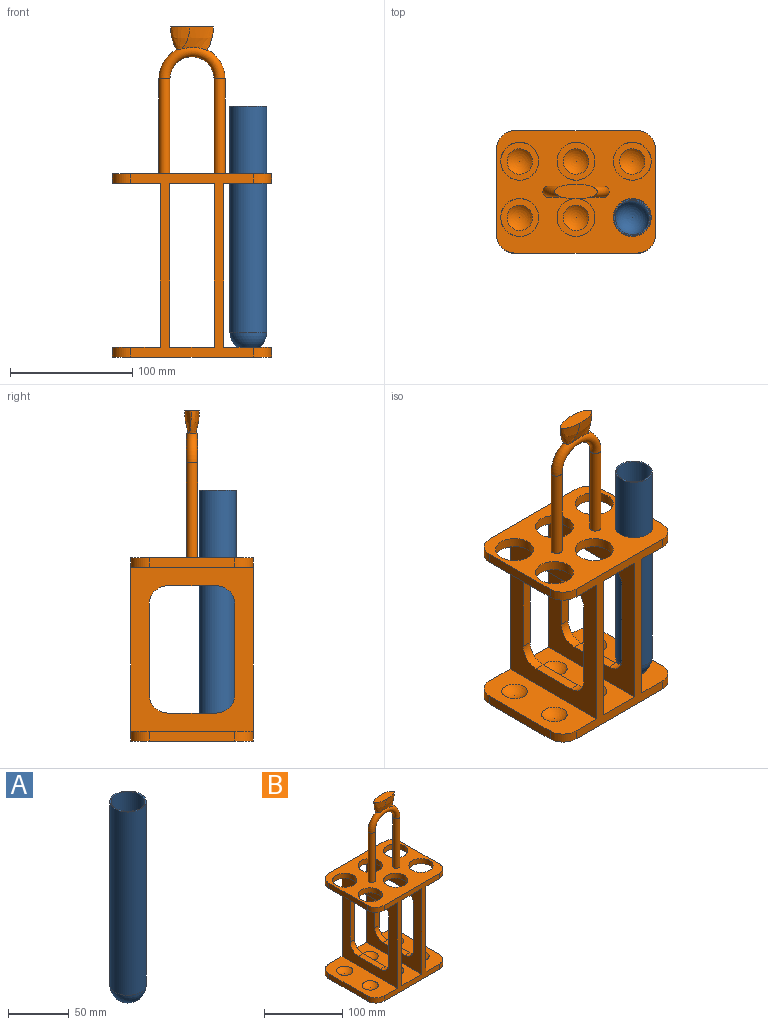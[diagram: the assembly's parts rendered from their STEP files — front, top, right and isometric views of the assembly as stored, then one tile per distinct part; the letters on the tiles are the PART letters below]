
ASSEMBLY  parts=2 mates=1
PART A: 5 faces, bbox 30x30x200 mm
  f0: plane 30x30mm, normal (0,0,1), area 91.1mm2, adj f1,f3
  f1: cylinder r=15mm len=185mm, axis (0,0,-1), area 17435.8mm2, adj f0,f2
  f2: sphere r=15mm, area 1413.7mm2, adj f1
  f3: cylinder r=14mm len=185mm, axis (0,0,-1), area 16273.4mm2, adj f0,f4
  f4: sphere r=14mm, area 1231.5mm2, adj f3
PART B: 62 faces, bbox 130.6x100.6x270.6 mm
  f0: plane 130x100mm, normal (0,0,1), area 8151mm2, adj f1,f3,f5,f7,f9,f15,f16,f26
  f1: cylinder r=15.5mm len=31mm, axis (0,0,-1), area 779.1mm2, adj f0,f25
  f2: sphere r=15.5mm, area 389.6mm2, adj f22
  f3: cylinder r=15.5mm len=31mm, axis (0,0,-1), area 779.1mm2, adj f0,f23
  f4: sphere r=15.5mm, area 389.6mm2, adj f24
  f5: cylinder r=15.5mm len=31mm, axis (0,0,-1), area 779.1mm2, adj f0,f17
  f6: sphere r=15.5mm, area 389.6mm2, adj f18
  f7: cylinder r=15.5mm len=31mm, axis (0,0,-1), area 779.1mm2, adj f0,f25
  f8: sphere r=15.5mm, area 389.6mm2, adj f22
  f9: cylinder r=15.5mm len=31mm, axis (0,0,-1), area 779.1mm2, adj f0,f23
  f10: sphere r=15.5mm, area 389.6mm2, adj f24
  f11: plane 134x100mm, normal (-1,0,0), area 6313.1mm2, adj f17,f18,f26,f27,f28,f29,f30,f31
  f12: plane 134x100mm, normal (1,0,0), area 6313.1mm2, adj f22,f25,f26,f27,f36,f37,f38,f39
  f13: plane 134x100mm, normal (-1,0,0), area 6313.1mm2, adj f23,f24,f26,f27,f36,f37,f38,f39
  f14: plane 134x100mm, normal (1,0,0), area 6313.1mm2, adj f23,f24,f26,f27,f28,f29,f30,f31
  f15: plane 70x8mm, normal (1,0,0), area 560mm2, adj f0,f25,f46,f50
  f16: plane 70x8mm, normal (-1,0,0), area 560mm2, adj f0,f17,f49,f53
  f17: plane 100x39mm, normal (0,0,-1), area 2293.9mm2, adj f5,f11,f16,f26,f27,f45,f49,f53
  f18: plane 100x39mm, normal (0,0,1), area 3124.8mm2, adj f6,f11,f19,f26,f27,f44,f48,f52
  f19: plane 70x8mm, normal (-1,0,0), area 560mm2, adj f18,f20,f48,f52
  f20: plane 130x100mm, normal (0,0,-1), area 12806.9mm2, adj f19,f21,f26,f27,f47,f48,f51,f52
  f21: plane 70x8mm, normal (1,0,0), area 560mm2, adj f20,f22,f47,f51
  f22: plane 100x39mm, normal (0,0,1), area 3124.8mm2, adj f2,f8,f12,f21,f26,f27,f47,f51
  f23: plane 100x36mm, normal (0,0,-1), area 2090.5mm2, adj f3,f9,f13,f14,f26,f27
  f24: plane 100x36mm, normal (0,0,1), area 2921.4mm2, adj f4,f10,f13,f14,f26,f27
  f25: plane 100x39mm, normal (0,0,-1), area 2293.9mm2, adj f1,f7,f12,f15,f26,f27,f46,f50
  f26: plane 150x100mm, normal (0,-1,0), area 3744mm2, adj f0,f11,f12,f13,f14,f17,f18,f20
  f27: plane 150x100mm, normal (0,1,0), area 3744mm2, adj f0,f11,f12,f13,f14,f17,f18,f20
  f28: cylinder r=15mm len=15mm, axis (1,0,0), area 188.5mm2, adj f11,f14,f29,f35
  f29: plane 74x8mm, normal (0,-1,0), area 592mm2, adj f11,f14,f28,f30
  f30: cylinder r=15mm len=15mm, axis (1,0,0), area 188.5mm2, adj f11,f14,f29,f31
  f31: plane 40x8mm, normal (0,0,1), area 320mm2, adj f11,f14,f30,f32
  f32: cylinder r=15mm len=15mm, axis (1,0,0), area 188.5mm2, adj f11,f14,f31,f33
  f33: plane 74x8mm, normal (0,1,0), area 592mm2, adj f11,f14,f32,f34
  f34: cylinder r=15mm len=15mm, axis (1,0,0), area 188.5mm2, adj f11,f14,f33,f35
  f35: plane 40x8mm, normal (0,0,-1), area 320mm2, adj f11,f14,f28,f34
  f36: plane 40x8mm, normal (0,0,-1), area 320mm2, adj f12,f13,f37,f43
  f37: cylinder r=15mm len=15mm, axis (1,0,0), area 188.5mm2, adj f12,f13,f36,f38
  f38: plane 74x8mm, normal (0,1,0), area 592mm2, adj f12,f13,f37,f39
  f39: cylinder r=15mm len=15mm, axis (1,0,0), area 188.5mm2, adj f12,f13,f38,f40
  f40: plane 40x8mm, normal (0,0,1), area 320mm2, adj f12,f13,f39,f41
  f41: cylinder r=15mm len=15mm, axis (1,0,0), area 188.5mm2, adj f12,f13,f40,f42
  f42: plane 74x8mm, normal (0,-1,0), area 592mm2, adj f12,f13,f41,f43
  f43: cylinder r=15mm len=15mm, axis (1,0,0), area 188.5mm2, adj f12,f13,f36,f42
  f44: sphere r=15.5mm, area 389.6mm2, adj f18
  f45: cylinder r=15.5mm len=31mm, axis (0,0,-1), area 779.1mm2, adj f0,f17
  f46: cylinder r=15mm len=15mm, axis (0,0,1), area 188.5mm2, adj f0,f15,f25,f27
  f47: cylinder r=15mm len=15mm, axis (0,0,1), area 188.5mm2, adj f20,f21,f22,f27
  f48: cylinder r=15mm len=15mm, axis (0,0,-1), area 188.5mm2, adj f18,f19,f20,f27
  f49: cylinder r=15mm len=15mm, axis (0,0,-1), area 188.5mm2, adj f0,f16,f17,f27
  f50: cylinder r=15mm len=15mm, axis (0,0,-1), area 188.5mm2, adj f0,f15,f25,f26
  f51: cylinder r=15mm len=15mm, axis (0,0,-1), area 188.5mm2, adj f20,f21,f22,f26
  f52: cylinder r=15mm len=15mm, axis (0,0,1), area 188.5mm2, adj f18,f19,f20,f26
  f53: cylinder r=15mm len=15mm, axis (0,0,1), area 188.5mm2, adj f0,f16,f17,f26
  f54: cylinder r=4.5mm len=77.5mm, axis (0,0,1), area 2191.3mm2, adj f0,f55
  f55: torus R=22.5mm, axis (0,1,0), area 1831.2mm2, adj f54,f56,f58,f59,f60,f61
  f56: cylinder r=4.5mm len=77.5mm, axis (0,0,-1), area 2191.3mm2, adj f0,f55
  f57: plane 35.64x12.62mm, normal (0,0,1), area 329.9mm2, adj f58,f59,f60,f61
  f58: bspline ~29.4x20mm, area 370.7mm2, adj f55,f57,f59,f61
  f59: bspline ~20x15.71mm, area 275.6mm2, adj f55,f57,f58,f60
  f60: bspline ~29.4x20mm, area 370.7mm2, adj f55,f57,f59,f61
  f61: bspline ~20x15.71mm, area 275.6mm2, adj f55,f57,f58,f60
PLACE A rot(axis=(0,0,1),11.8deg) t=(46,-71,5)mm
PLACE B at identity fixed
MATE cylindrical A.f1 <-> B.f1  axis (0,0,-1) through (46,-71,112.5)mm
